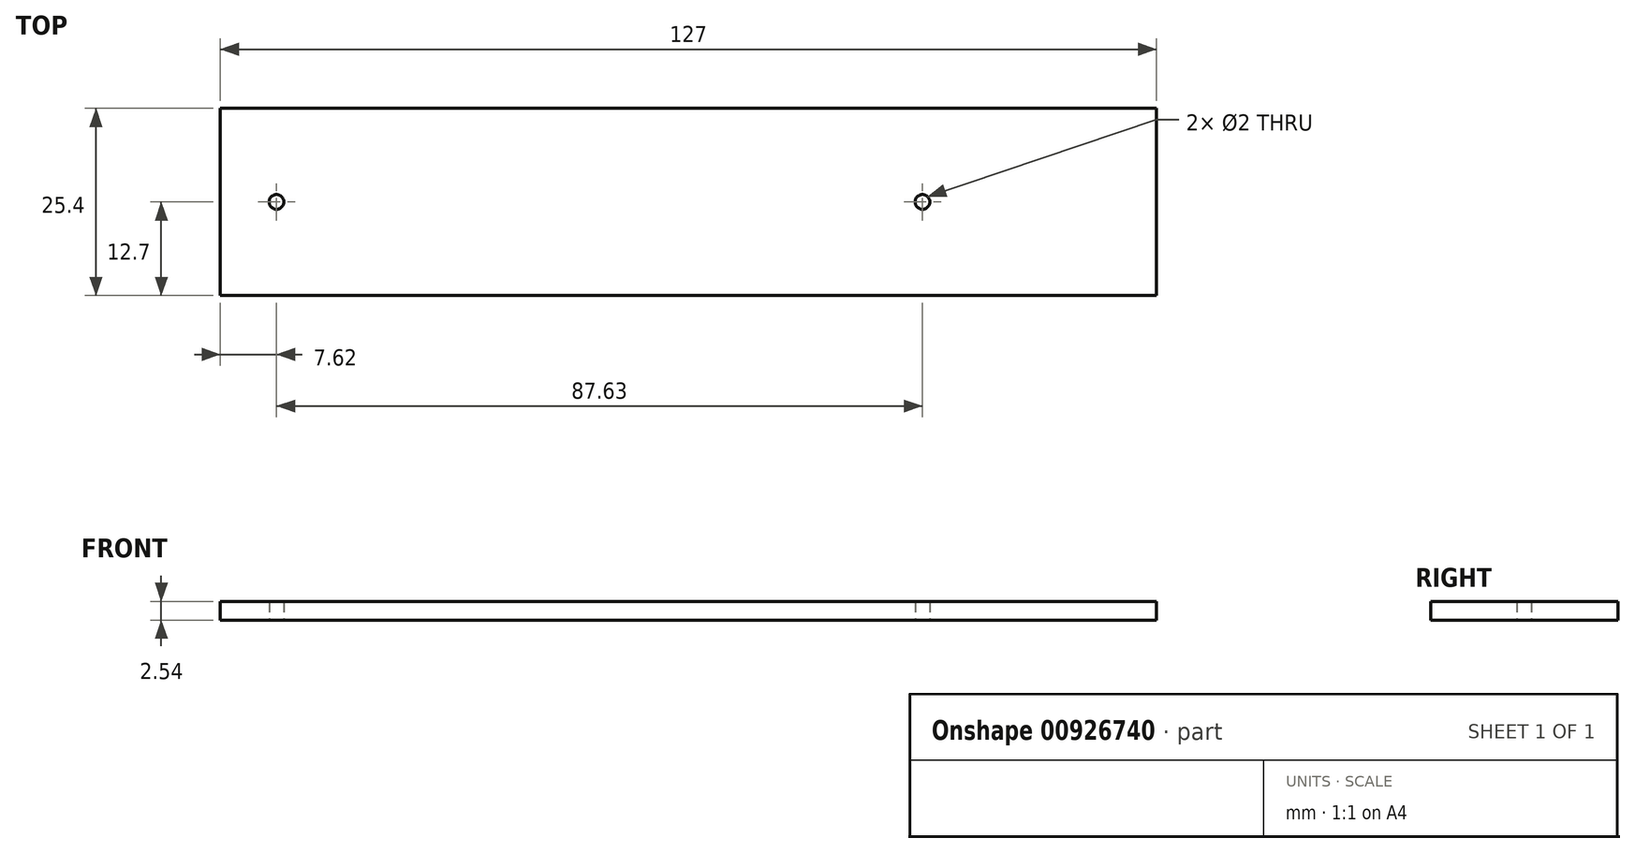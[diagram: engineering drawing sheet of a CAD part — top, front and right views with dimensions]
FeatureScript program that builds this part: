
annotation { "Feature Type Name" : "Feature", "Feature Type Description" : "" }
export const myFeature = defineFeature(function(context is Context, id is Id, definition is map)
    precondition{}
    {
        {
            var Q0;
            Q0=qCreatedBy(makeId("Top.planeOp"),FACE);
            var sketch = newSketch(context, id + "F0", { "sketchPlane" : qUnion([Q0])});
            skLineSegment(sketch, "E0.bottom", {"start": v(63.5, 12.7) * mm, "end": v(-63.5, 12.7) * mm});
            skLineSegment(sketch, "E0.top", {"start": v(63.5, -12.7) * mm, "end": v(-63.5, -12.7) * mm});
            skLineSegment(sketch, "E0.left", {"start": v(63.5, 12.7) * mm, "end": v(63.5, -12.7) * mm});
            skLineSegment(sketch, "E0.right", {"start": v(-63.5, 12.7) * mm, "end": v(-63.5, -12.7) * mm});
            skPoint(sketch, "E0.middle", {"position": v(0, 0) * mm});
            skCircle(sketch, "E1", {"center": v(-55.88, 0) * mm, "radius": 1 * mm});
            skCircle(sketch, "E2", {"center": v(31.75, 0) * mm, "radius": 1 * mm});
            skPoint(sketch, "E3.orphan", {"position": v(63.5, 0) * mm});
            skPoint(sketch, "E4.end.orphan", {"position": v(0, 12.7) * mm});
            skSolve(sketch);
        }
        {
            var Q0;
            Q0 = qSketchRegion(id + "F0", true);
            extrude(context, id + "F1", {"entities" : qUnion([Q0]), "endBound" : BoundingType.SYMMETRIC, "depth" : 2.54 * mm, "offsetDistance" : 25.4 * mm});
        }
    });
